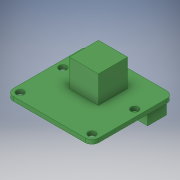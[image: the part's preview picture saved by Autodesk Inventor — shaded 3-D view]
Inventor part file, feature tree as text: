
AUTODESK INVENTOR PART (.ipt)
format: ipt  version: 2019 (Build 230136000, 136)  size: 152,576 bytes
history: native  units: mm
features: extrude x3, sketch x3
ambient origin geometry x8: Origin, YZ Plane, XZ Plane, XY Plane, X Axis, Y Axis, Z Axis, Center Point
bodies: Solid1 (feature_tree)
feature tree (6):
  extrude  "Extrusion1"  Depth=23.862mm
  extrude  "Extrusion2"  Depth=2.0mm
  extrude  "Extrusion3"  Depth=2.0mm
  sketch  "Sketch1"  dims[d0=25.0mm d1=23.862mm]
  sketch  "Sketch2"  dims[d2=2.0mm d3=2.0mm]
  sketch  "Sketch3"  dims[d4=14.5mm d5=2.0mm d6=2.0mm d7=2.2mm d8=2.2mm d9=2.2mm d10=2.2mm d11=1.2mm d12=0.0mm d13=8.5mm d14=8.5mm d15=12.5mm d16=9.462mm d17=8.0mm d18=0.0mm d19=20.8mm d20=5.5mm d21=5.0mm d22=0.0mm]
